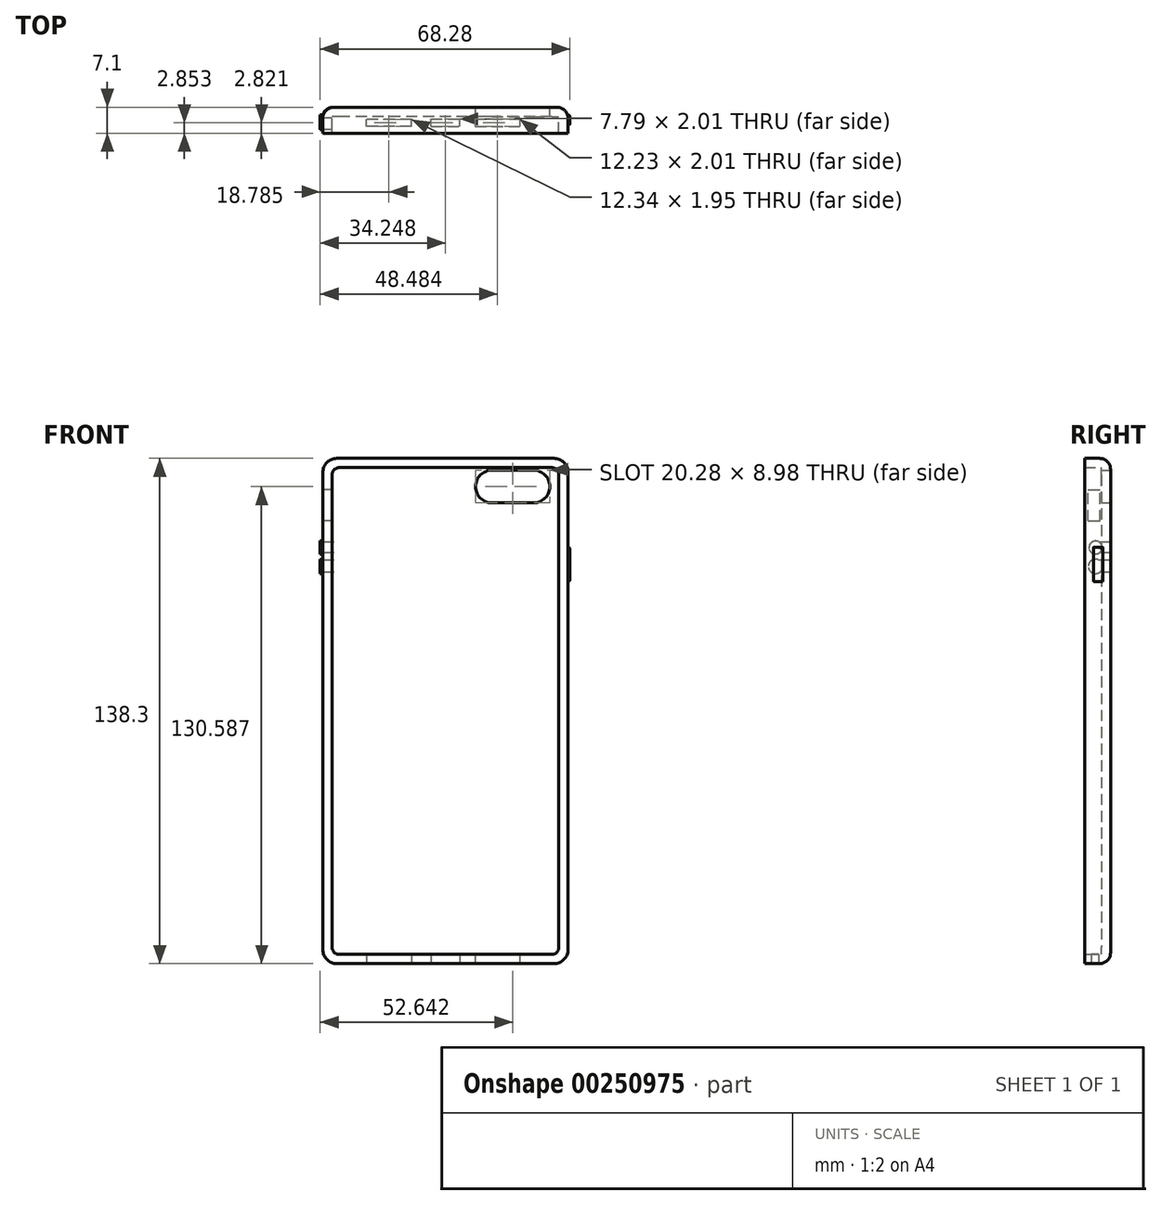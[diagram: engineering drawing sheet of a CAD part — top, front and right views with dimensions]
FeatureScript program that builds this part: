
annotation { "Feature Type Name" : "Feature", "Feature Type Description" : "" }
export const myFeature = defineFeature(function(context is Context, id is Id, definition is map)
    precondition{}
    {
        {
            var Q0;
            Q0=qCreatedBy(makeId("Front.planeOp"),FACE);
            var sketch = newSketch(context, id + "F0", { "sketchPlane" : qUnion([Q0])});
            skLineSegment(sketch, "E0.bottom", {"start": v(33.55, 69.15) * mm, "end": v(-33.55, 69.15) * mm});
            skLineSegment(sketch, "E0.top", {"start": v(33.55, -69.15) * mm, "end": v(-33.55, -69.15) * mm});
            skLineSegment(sketch, "E0.left", {"start": v(33.55, 69.15) * mm, "end": v(33.55, -69.15) * mm});
            skLineSegment(sketch, "E0.right", {"start": v(-33.55, 69.15) * mm, "end": v(-33.55, -69.15) * mm});
            skPoint(sketch, "E0.middle", {"position": v(0, 0) * mm});
            skSolve(sketch);
        }
        {
            var Q0;
            Q0=makeQuery(id+"F0.imprint","IMPRINT",FACE,{"disambiguationData":[TD([[makeQuery(id+"F0.imprint","IMPRINT",EDGE,{"derivedFrom":sQuery(id+"F0.wireOp",EDGE,"E0.bottom")}),1.0]])]});
            extrude(context, id + "F1", {"entities" : qUnion([Q0]), "endBound" : BoundingType.SYMMETRIC, "depth" : 7.1 * mm});
        }
        {
            var Q0;
            Q0=makeQuery(id+"F1.opExtrude","CAP_FACE",FACE,{"disambiguationData":[OSD([sQuery(id+"F0.wireOp",EDGE,"E0.bottom"),sQuery(id+"F0.wireOp",EDGE,"E0.top"),sQuery(id+"F0.wireOp",EDGE,"E0.left"),sQuery(id+"F0.wireOp",EDGE,"E0.right")])],"isStart":false});
            shell(context, id + "F2", {"entities" : qUnion([Q0]), "thickness" : 2.54 * mm});
        }
        {
            var Q0;
            Q0=makeQuery(id+"F1.opExtrude","SWEPT_EDGE",EDGE,{"disambiguationData":[OSD([sQuery(id+"F0.wireOp",EDGE,"E0.bottom"),sQuery(id+"F0.wireOp",EDGE,"E0.right")])]});
            var Q1;
            Q1=makeQuery(id+"F1.opExtrude","SWEPT_EDGE",EDGE,{"disambiguationData":[OSD([sQuery(id+"F0.wireOp",EDGE,"E0.bottom"),sQuery(id+"F0.wireOp",EDGE,"E0.left")])]});
            var Q2;
            Q2=makeQuery(id+"F1.opExtrude","SWEPT_EDGE",EDGE,{"disambiguationData":[OSD([sQuery(id+"F0.wireOp",EDGE,"E0.top"),sQuery(id+"F0.wireOp",EDGE,"E0.left")])]});
            var Q3;
            Q3=makeQuery(id+"F1.opExtrude","SWEPT_EDGE",EDGE,{"disambiguationData":[OSD([sQuery(id+"F0.wireOp",EDGE,"E0.top"),sQuery(id+"F0.wireOp",EDGE,"E0.right")])]});
            fillet(context, id + "F3", {"entities" : qUnion([Q0, Q1, Q2, Q3]), "radius" : 3.86 * mm, "tangentPropagation" : true, "allowEdgeOverflow" : false});
        }
        {
            var Q0;
            Q0=makeQuery(id+"F1.opExtrude","CAP_FACE",FACE,{"disambiguationData":[OSD([sQuery(id+"F0.wireOp",EDGE,"E0.bottom"),sQuery(id+"F0.wireOp",EDGE,"E0.top"),sQuery(id+"F0.wireOp",EDGE,"E0.left"),sQuery(id+"F0.wireOp",EDGE,"E0.right")])],"isStart":true});
            var sketch = newSketch(context, id + "F4", { "sketchPlane" : qUnion([Q0])});
            skLineSegment(sketch, "E1.bottom", {"start": v(-24.04, 65.93) * mm, "end": v(-12.74, 65.93) * mm});
            skLineSegment(sketch, "E1.top", {"start": v(-24.04, 56.95) * mm, "end": v(-12.74, 56.95) * mm});
            skLineSegment(sketch, "E1.left", {"start": v(-24.04, 65.93) * mm, "end": v(-24.04, 56.95) * mm});
            skLineSegment(sketch, "E1.right", {"start": v(-12.74, 65.93) * mm, "end": v(-12.74, 56.95) * mm});
            skArc(sketch, "E2", {"start": v(-12.74, 56.95) * mm, "mid": v(-8.25, 61.44) * mm, "end": v(-12.74, 65.93) * mm});
            skArc(sketch, "E3", {"start": v(-24.04, 65.93) * mm, "mid": v(-28.53, 61.44) * mm, "end": v(-24.04, 56.95) * mm});
            skSolve(sketch);
        }
        {
            var Q0;
            Q0=makeQuery(id+"F4.imprint","IMPRINT",FACE,{"disambiguationData":[TD([[makeQuery(id+"F4.imprint","IMPRINT",EDGE,{"derivedFrom":sQuery(id+"F4.wireOp",EDGE,"E1.left")}),-1.0]])]});
            var Q1;
            Q1=makeQuery(id+"F4.imprint","IMPRINT",FACE,{"disambiguationData":[TD([[makeQuery(id+"F4.imprint","IMPRINT",EDGE,{"derivedFrom":sQuery(id+"F4.wireOp",EDGE,"E1.bottom")}),-1.0]])]});
            var Q2;
            Q2=makeQuery(id+"F4.imprint","IMPRINT",FACE,{"disambiguationData":[TD([[makeQuery(id+"F4.imprint","IMPRINT",EDGE,{"derivedFrom":sQuery(id+"F4.wireOp",EDGE,"E1.right")}),1.0]])]});
            extrude(context, id + "F5", {"entities" : qUnion([Q0, Q1, Q2]), "operationType" : NewBodyOperationType.REMOVE, "oppositeDirection" : true, "depth" : 25 * mm});
        }
        {
            var Q0;
            Q0=makeQuery(id+"F1.opExtrude","SWEPT_FACE",FACE,{"disambiguationData":[OSD([sQuery(id+"F0.wireOp",EDGE,"E0.top")])]});
            var sketch = newSketch(context, id + "F6", { "sketchPlane" : qUnion([Q0])});
            skLineSegment(sketch, "E4.bottom", {"start": v(-3.9, 1.7) * mm, "end": v(3.9, 1.7) * mm});
            skLineSegment(sketch, "E4.top", {"start": v(-3.9, -0.3) * mm, "end": v(3.9, -0.3) * mm});
            skLineSegment(sketch, "E4.left", {"start": v(-3.9, 1.7) * mm, "end": v(-3.9, -0.3) * mm});
            skLineSegment(sketch, "E4.right", {"start": v(3.9, 1.7) * mm, "end": v(3.9, -0.3) * mm});
            skSolve(sketch);
        }
        {
            var Q0;
            Q0=makeQuery(id+"F6.imprint","IMPRINT",FACE,{"disambiguationData":[TD([[makeQuery(id+"F6.imprint","IMPRINT",EDGE,{"derivedFrom":sQuery(id+"F6.wireOp",EDGE,"E4.bottom")}),-1.0]])]});
            extrude(context, id + "F7", {"entities" : qUnion([Q0]), "operationType" : NewBodyOperationType.REMOVE, "endBound" : BoundingType.SYMMETRIC, "oppositeDirection" : true, "depth" : 25 * mm});
        }
        {
            var Q0;
            Q0=makeQuery(id+"F2.opShell","OFFSET_EDGE",EDGE,{"disambiguationData":[OSD([sQuery(id+"F0.wireOp",EDGE,"E0.bottom"),sQuery(id+"F0.wireOp",EDGE,"E0.right")])]});
            var Q1;
            Q1=makeQuery(id+"F2.opShell","OFFSET_EDGE",EDGE,{"disambiguationData":[OSD([sQuery(id+"F0.wireOp",EDGE,"E0.bottom"),sQuery(id+"F0.wireOp",EDGE,"E0.left")])]});
            var Q2;
            Q2=makeQuery(id+"F2.opShell","OFFSET_EDGE",EDGE,{"disambiguationData":[OSD([sQuery(id+"F0.wireOp",EDGE,"E0.top"),sQuery(id+"F0.wireOp",EDGE,"E0.right")])]});
            var Q3;
            Q3=makeQuery(id+"F2.opShell","OFFSET_EDGE",EDGE,{"disambiguationData":[OSD([sQuery(id+"F0.wireOp",EDGE,"E0.top"),sQuery(id+"F0.wireOp",EDGE,"E0.left")])]});
            fillet(context, id + "F8", {"entities" : qUnion([Q0, Q1, Q2, Q3]), "radius" : 1.93 * mm, "tangentPropagation" : true, "allowEdgeOverflow" : false});
        }
        {
            var Q0;
            Q0=makeQuery(id+"F1.opExtrude","SWEPT_FACE",FACE,{"disambiguationData":[OSD([sQuery(id+"F0.wireOp",EDGE,"E0.right")])]});
            var sketch = newSketch(context, id + "F9", { "sketchPlane" : qUnion([Q0])});
            skLineSegment(sketch, "E5.bottom", {"start": v(-0.62, 60.6) * mm, "end": v(2.6, 60.6) * mm});
            skLineSegment(sketch, "E5.top", {"start": v(-0.62, 52.03) * mm, "end": v(2.6, 52.03) * mm});
            skLineSegment(sketch, "E5.left", {"start": v(-0.62, 60.6) * mm, "end": v(-0.62, 52.03) * mm});
            skLineSegment(sketch, "E5.right", {"start": v(2.6, 60.6) * mm, "end": v(2.6, 52.03) * mm});
            skSolve(sketch);
        }
        {
            var Q0;
            Q0=makeQuery(id+"F9.imprint","IMPRINT",FACE,{"disambiguationData":[TD([[makeQuery(id+"F9.imprint","IMPRINT",EDGE,{"derivedFrom":sQuery(id+"F9.wireOp",EDGE,"E5.bottom")}),-1.0]])]});
            extrude(context, id + "F10", {"entities" : qUnion([Q0]), "operationType" : NewBodyOperationType.REMOVE, "endBound" : BoundingType.SYMMETRIC, "oppositeDirection" : true, "depth" : 71.4 * mm});
        }
        {
            var Q0;
            Q0=makeQuery(id+"F1.opExtrude","SWEPT_FACE",FACE,{"disambiguationData":[OSD([sQuery(id+"F0.wireOp",EDGE,"E0.left")])]});
            var sketch = newSketch(context, id + "F11", { "sketchPlane" : qUnion([Q0])});
            skLineSegment(sketch, "E6.bottom", {"start": v(-1.1, 44.83) * mm, "end": v(1.39, 44.83) * mm});
            skLineSegment(sketch, "E6.top", {"start": v(-1.1, 35.48) * mm, "end": v(1.39, 35.48) * mm});
            skLineSegment(sketch, "E6.left", {"start": v(-1.1, 44.83) * mm, "end": v(-1.1, 35.48) * mm});
            skLineSegment(sketch, "E6.right", {"start": v(1.39, 44.83) * mm, "end": v(1.39, 35.48) * mm});
            skSolve(sketch);
        }
        {
            var Q0;
            Q0=makeQuery(id+"F11.imprint","IMPRINT",FACE,{"disambiguationData":[TD([[makeQuery(id+"F11.imprint","IMPRINT",EDGE,{"derivedFrom":sQuery(id+"F11.wireOp",EDGE,"E6.bottom")}),-1.0]])]});
            extrude(context, id + "F12", {"entities" : qUnion([Q0]), "operationType" : NewBodyOperationType.ADD, "endBound" : BoundingType.SYMMETRIC, "depth" : 0.96 * mm});
        }
        {
            var Q0;
            Q0=makeQuery(id+"F1.opExtrude","SWEPT_FACE",FACE,{"disambiguationData":[OSD([sQuery(id+"F0.wireOp",EDGE,"E0.right")])]});
            var sketch = newSketch(context, id + "F13", { "sketchPlane" : qUnion([Q0])});
            skCircle(sketch, "E7", {"center": v(0.53, 44.75) * mm, "radius": 1.78 * mm});
            skPoint(sketch, "E7.first.point", {"position": v(1.78, 46.02) * mm});
            skPoint(sketch, "E7.second.point", {"position": v(-1.2, 44.39) * mm});
            skPoint(sketch, "E7.third.point", {"position": v(1.98, 43.7) * mm});
            skCircle(sketch, "E8", {"center": v(0.55, 39.58) * mm, "radius": 1.97 * mm});
            skPoint(sketch, "E8.first.point", {"position": v(-1.11, 40.63) * mm});
            skPoint(sketch, "E8.second.point", {"position": v(2.17, 38.45) * mm});
            skPoint(sketch, "E8.third.point", {"position": v(-1.02, 38.38) * mm});
            skSolve(sketch);
        }
        {
            var Q0;
            Q0=makeQuery(id+"F13.imprint","IMPRINT",FACE,{"disambiguationData":[TD([[makeQuery(id+"F13.imprint","IMPRINT",EDGE,{"derivedFrom":sQuery(id+"F13.wireOp",EDGE,"E7")}),1.0]])]});
            var Q1;
            Q1=makeQuery(id+"F13.imprint","IMPRINT",FACE,{"disambiguationData":[TD([[makeQuery(id+"F13.imprint","IMPRINT",EDGE,{"derivedFrom":sQuery(id+"F13.wireOp",EDGE,"E8")}),1.0]])]});
            extrude(context, id + "F14", {"entities" : qUnion([Q0, Q1]), "operationType" : NewBodyOperationType.ADD, "endBound" : BoundingType.SYMMETRIC, "depth" : 1.4 * mm});
        }
        {
            var Q0;
            Q0=makeQuery(id+"F1.opExtrude","SWEPT_FACE",FACE,{"disambiguationData":[OSD([sQuery(id+"F0.wireOp",EDGE,"E0.top")])]});
            var sketch = newSketch(context, id + "F15", { "sketchPlane" : qUnion([Q0])});
            skLineSegment(sketch, "E9.bottom", {"start": v(-9.3, 1.7) * mm, "end": v(-21.64, 1.7) * mm});
            skLineSegment(sketch, "E9.top", {"start": v(-9.3, -0.25) * mm, "end": v(-21.64, -0.25) * mm});
            skLineSegment(sketch, "E9.left", {"start": v(-9.3, 1.7) * mm, "end": v(-9.3, -0.25) * mm});
            skLineSegment(sketch, "E9.right", {"start": v(-21.64, 1.7) * mm, "end": v(-21.64, -0.25) * mm});
            skLineSegment(sketch, "E10.bottom", {"start": v(8.12, -0.3) * mm, "end": v(20.35, -0.3) * mm});
            skLineSegment(sketch, "E10.top", {"start": v(8.12, 1.7) * mm, "end": v(20.35, 1.7) * mm});
            skLineSegment(sketch, "E10.left", {"start": v(8.12, -0.3) * mm, "end": v(8.12, 1.7) * mm});
            skLineSegment(sketch, "E10.right", {"start": v(20.35, -0.3) * mm, "end": v(20.35, 1.7) * mm});
            skSolve(sketch);
        }
        {
            var Q0;
            Q0=makeQuery(id+"F15.imprint","IMPRINT",FACE,{"disambiguationData":[TD([[makeQuery(id+"F15.imprint","IMPRINT",EDGE,{"derivedFrom":sQuery(id+"F15.wireOp",EDGE,"E9.bottom")}),1.0]])]});
            var Q1;
            Q1=makeQuery(id+"F15.imprint","IMPRINT",FACE,{"disambiguationData":[TD([[makeQuery(id+"F15.imprint","IMPRINT",EDGE,{"derivedFrom":sQuery(id+"F15.wireOp",EDGE,"E10.bottom")}),1.0]])]});
            extrude(context, id + "F16", {"entities" : qUnion([Q0, Q1]), "operationType" : NewBodyOperationType.REMOVE, "endBound" : BoundingType.SYMMETRIC, "oppositeDirection" : true, "depth" : 25 * mm});
        }
        {
            var Q0;
            Q0=makeQuery(id+"F1.opExtrude","CAP_EDGE",EDGE,{"disambiguationData":[OSD([sQuery(id+"F0.wireOp",EDGE,"E0.left")])],"isStart":true});
            fillet(context, id + "F17", {"entities" : qUnion([Q0]), "radius" : 3 * mm, "tangentPropagation" : true, "allowEdgeOverflow" : false});
        }
        {
            var Q0;
            Q0=makeQuery(id+"F12.opExtrude","CAP_EDGE",EDGE,{"disambiguationData":[OSD([sQuery(id+"F11.wireOp",EDGE,"E6.top")])],"isStart":false});
            var Q1;
            Q1=makeQuery(id+"F12.opExtrude","CAP_EDGE",EDGE,{"disambiguationData":[OSD([sQuery(id+"F11.wireOp",EDGE,"E6.bottom")])],"isStart":false});
            var Q2;
            Q2=makeQuery(id+"F12.opExtrude","CAP_EDGE",EDGE,{"disambiguationData":[OSD([sQuery(id+"F11.wireOp",EDGE,"E6.right")])],"isStart":false});
            fillet(context, id + "F18", {"entities" : qUnion([Q0, Q1, Q2]), "radius" : 0.46 * mm, "tangentPropagation" : true, "allowEdgeOverflow" : false});
        }
    });
